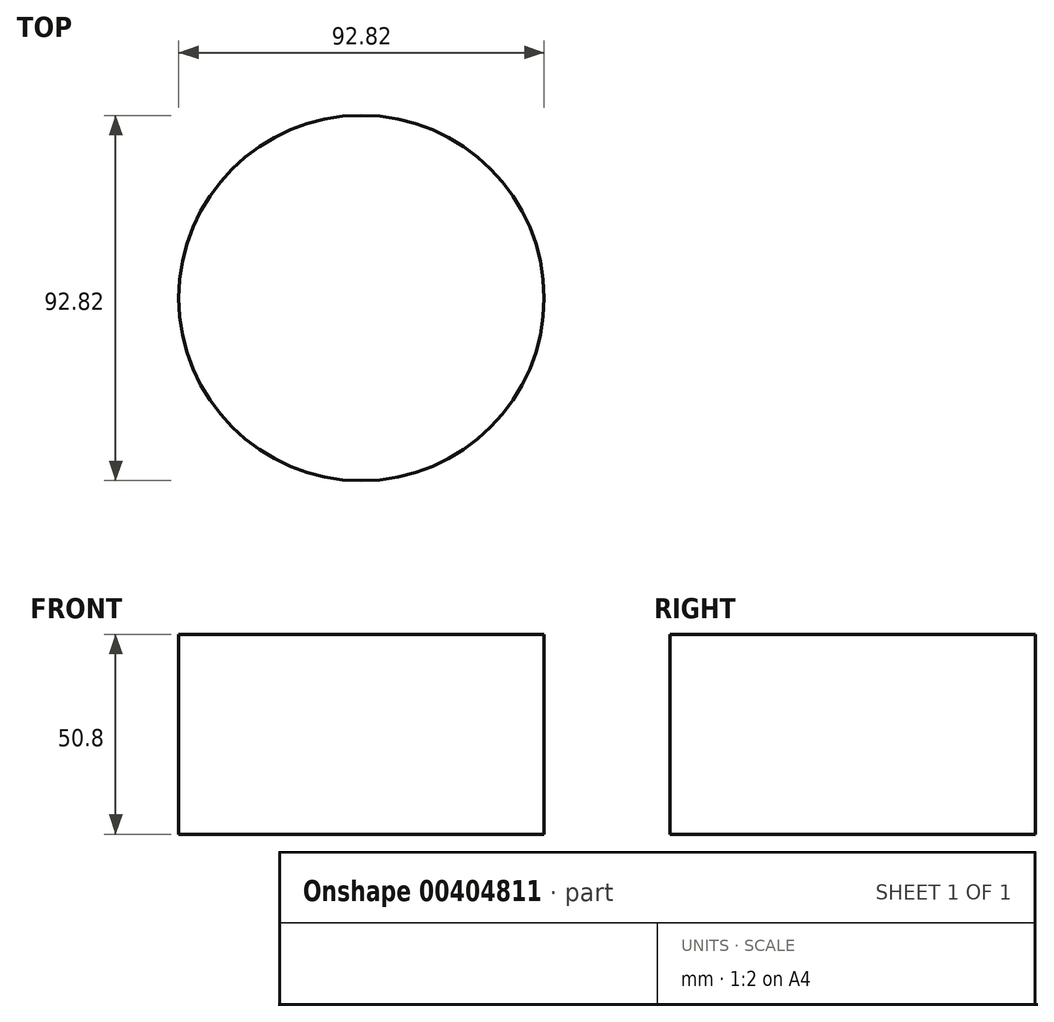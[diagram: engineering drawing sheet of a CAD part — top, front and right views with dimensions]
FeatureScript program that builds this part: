
annotation { "Feature Type Name" : "Feature", "Feature Type Description" : "" }
export const myFeature = defineFeature(function(context is Context, id is Id, definition is map)
    precondition{}
    {
        {
            var Q0;
            Q0=qCreatedBy(makeId("Top.planeOp"),FACE);
            var sketch = newSketch(context, id + "F0", { "sketchPlane" : qUnion([Q0])});
            skCircle(sketch, "E0", {"center": v(0, 0) * mm, "radius": 46.4 * mm});
            skSolve(sketch);
        }
        {
            var Q0;
            Q0=makeQuery(id+"F0.imprint","IMPRINT",FACE,{"disambiguationData":[TD([[makeQuery(id+"F0.imprint","IMPRINT",EDGE,{"derivedFrom":sQuery(id+"F0.wireOp",EDGE,"E0")}),1.0]])]});
            extrude(context, id + "F1", {"entities" : qUnion([Q0]), "depth" : 50.8 * mm});
        }
    });
